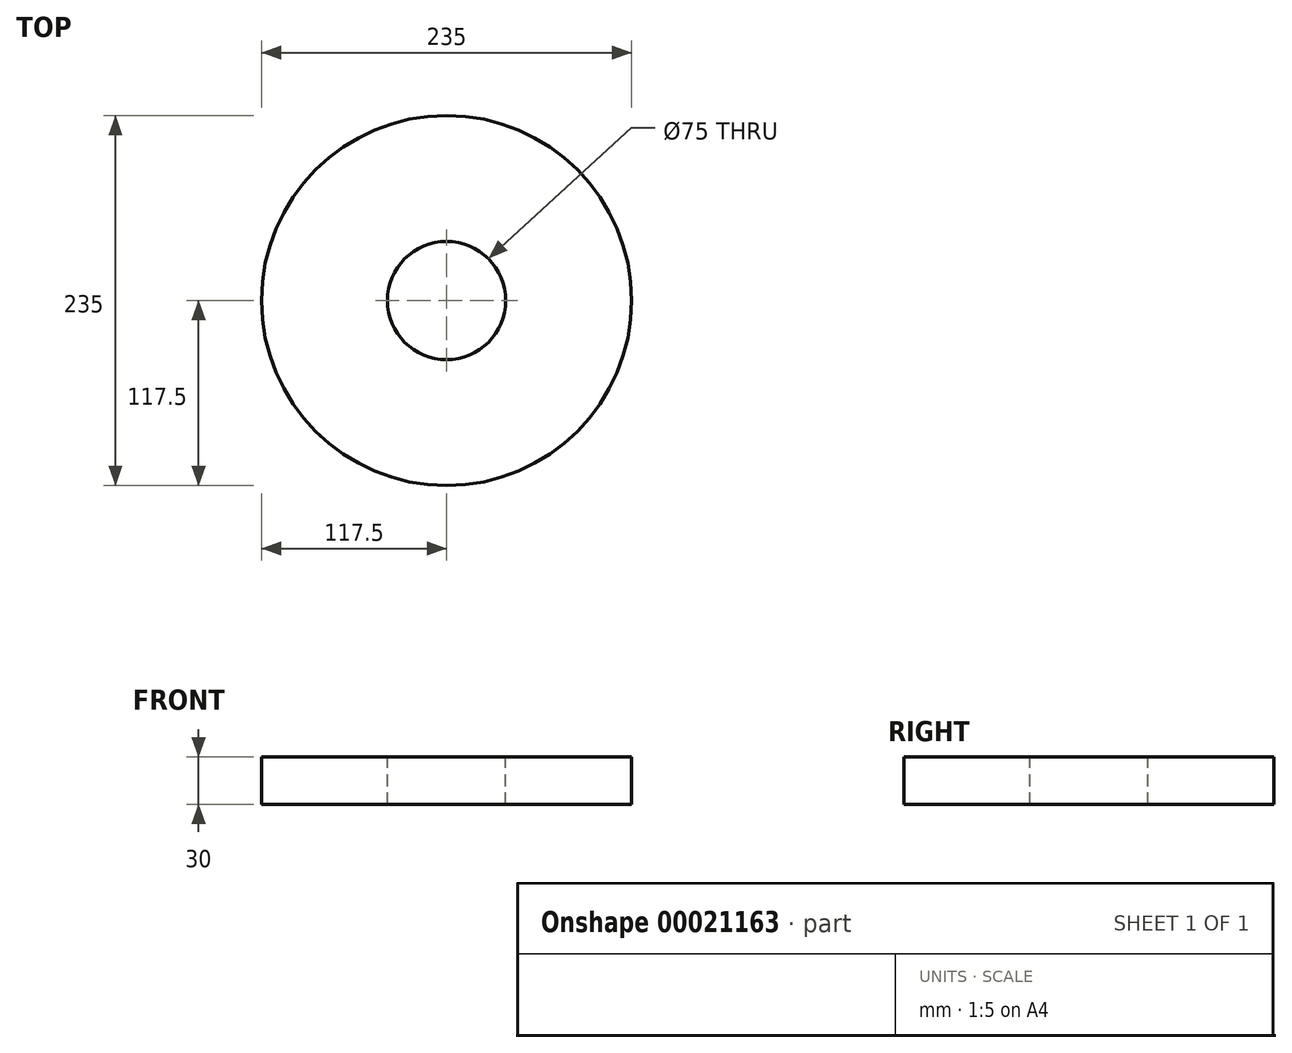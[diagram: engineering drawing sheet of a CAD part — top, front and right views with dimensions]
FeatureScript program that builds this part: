
annotation { "Feature Type Name" : "Feature", "Feature Type Description" : "" }
export const myFeature = defineFeature(function(context is Context, id is Id, definition is map)
    precondition{}
    {
        {
            var Q0;
            Q0=qCreatedBy(makeId("Top.planeOp"),FACE);
            var sketch = newSketch(context, id + "F0", { "sketchPlane" : qUnion([Q0])});
            skCircle(sketch, "E0", {"center": v(0, 0) * mm, "radius": 117.5 * mm});
            skSolve(sketch);
        }
        {
            var Q0;
            Q0 = qSketchRegion(id + "F0", true);
            extrude(context, id + "F1", {"entities" : qUnion([Q0]), "oppositeDirection" : true, "depth" : 30 * mm});
        }
        {
            var Q0;
            Q0=makeQuery(id+"F1.opExtrude","CAP_FACE",FACE,{"disambiguationData":[OSD([sQuery(id+"F0.wireOp",EDGE,"E0")])],"isStart":true});
            var sketch = newSketch(context, id + "F2", { "sketchPlane" : qUnion([Q0])});
            skCircle(sketch, "E1", {"center": v(0, 0) * mm, "radius": 37.5 * mm});
            skSolve(sketch);
        }
        {
            var Q0;
            Q0 = qSketchRegion(id + "F2", true);
            extrude(context, id + "F3", {"entities" : qUnion([Q0]), "operationType" : NewBodyOperationType.REMOVE, "endBound" : BoundingType.UP_TO_NEXT, "oppositeDirection" : true, "depth" : 25 * mm});
        }
    });
